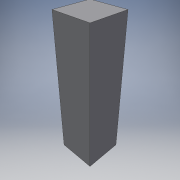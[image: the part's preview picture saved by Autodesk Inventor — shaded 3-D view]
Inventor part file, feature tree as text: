
AUTODESK INVENTOR PART (.ipt)
format: ipt  version: 2016 (Build 200138000, 138)  size: 86,528 bytes
history: native  units: in
note: dims shown in document units (in); Inventor stores cm internally (conversion verified against a paired STEP export)
features: extrude x1, sketch x1
ambient origin geometry x8: Origin, YZ Plane, XZ Plane, XY Plane, X Axis, Y Axis, Z Axis, Center Point
bodies: Solid1 (feature_tree)
feature tree (2):
  extrude  "Extrusion1"  Depth=1.5in
  sketch  "Sketch1"  dims[d0=1.5in d1=1.5in d2=5.5in d3=0.0in]
